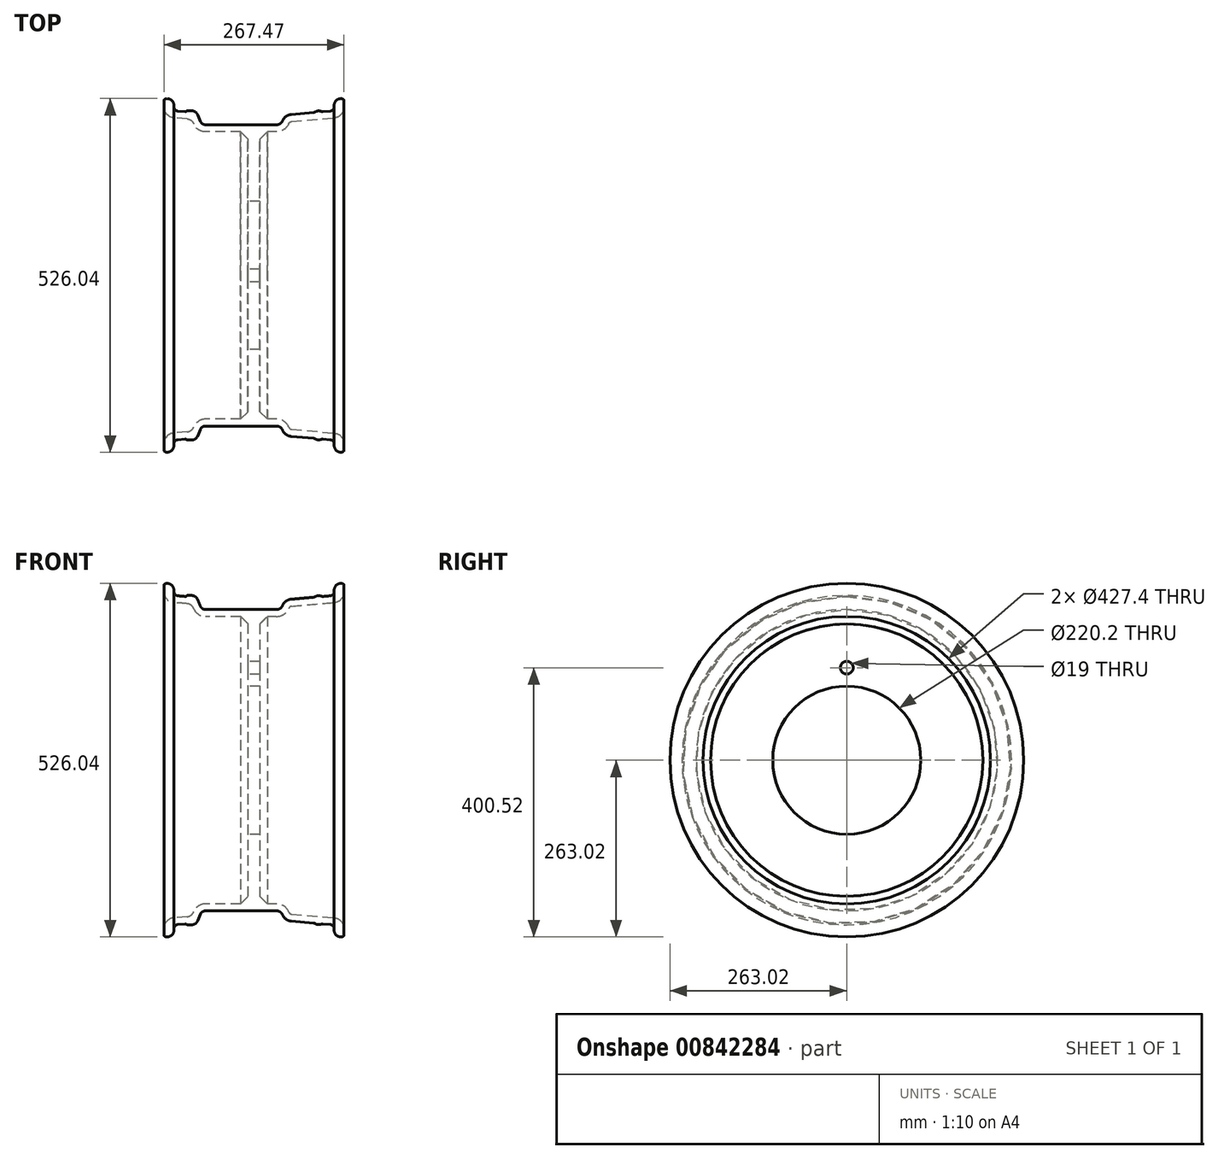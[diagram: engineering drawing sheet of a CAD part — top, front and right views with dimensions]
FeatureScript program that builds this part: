
annotation { "Feature Type Name" : "Feature", "Feature Type Description" : "" }
export const myFeature = defineFeature(function(context is Context, id is Id, definition is map)
    precondition{}
    {
        {
            var Q0;
            Q0=qCreatedBy(makeId("Front.planeOp"),FACE);
            var sketch = newSketch(context, id + "F0", { "sketchPlane" : qUnion([Q0])});
            skArc(sketch, "E0", {"start": v(-59.38, 126.45) * mm, "mid": v(-60.86, 130.03) * mm, "end": v(-64.44, 131.51) * mm});
            skArc(sketch, "E1", {"start": v(-64.44, 131.51) * mm, "mid": v(-65.43, 131.36) * mm, "end": v(-66.34, 130.91) * mm});
            skArc(sketch, "E2", {"start": v(-66.34, 130.91) * mm, "mid": v(-66.59, 130.63) * mm, "end": v(-66.68, 130.27) * mm});
            skArc(sketch, "E3", {"start": v(-66.68, 125.06) * mm, "mid": v(-64.62, 119.78) * mm, "end": v(-59.54, 117.27) * mm});
            skLineSegment(sketch, "E4", {"start": v(-59.54, 117.27) * mm, "end": v(-49.6, 116.4) * mm});
            skArc(sketch, "E5", {"start": v(-44.62, 112.72) * mm, "mid": v(-46.59, 115.26) * mm, "end": v(-49.6, 116.4) * mm});
            skArc(sketch, "E6", {"start": v(-44.62, 112.72) * mm, "mid": v(-41.16, 108.45) * mm, "end": v(-35.91, 106.85) * mm});
            skLineSegment(sketch, "E7", {"start": v(-39.78, 114.67) * mm, "end": v(-41.66, 119.33) * mm});
            skArc(sketch, "E8", {"start": v(-41.66, 119.33) * mm, "mid": v(-43.52, 121.63) * mm, "end": v(-46.35, 122.5) * mm});
            skLineSegment(sketch, "E9", {"start": v(-49.21, 122.5) * mm, "end": v(-46.35, 122.5) * mm});
            skArc(sketch, "E10", {"start": v(-49.21, 122.5) * mm, "mid": v(-49.52, 122.43) * mm, "end": v(-49.78, 122.25) * mm});
            skArc(sketch, "E11", {"start": v(-51.05, 121.76) * mm, "mid": v(-50.36, 121.86) * mm, "end": v(-49.78, 122.25) * mm});
            skLineSegment(sketch, "E12", {"start": v(-56.52, 122.24) * mm, "end": v(-51.05, 121.76) * mm});
            skArc(sketch, "E13", {"start": v(-59.38, 125.36) * mm, "mid": v(-58.56, 123.25) * mm, "end": v(-56.52, 122.24) * mm});
            skArc(sketch, "E14", {"start": v(56.9, 122.24) * mm, "mid": v(58.94, 123.25) * mm, "end": v(59.76, 125.36) * mm});
            skLineSegment(sketch, "E15", {"start": v(51.55, 121.77) * mm, "end": v(56.9, 122.24) * mm});
            skArc(sketch, "E16", {"start": v(50.11, 121.99) * mm, "mid": v(50.82, 121.8) * mm, "end": v(51.55, 121.77) * mm});
            skArc(sketch, "E17", {"start": v(50.11, 121.99) * mm, "mid": v(47.86, 122.32) * mm, "end": v(45.7, 121.6) * mm});
            skArc(sketch, "E18", {"start": v(44.33, 121.14) * mm, "mid": v(45.05, 121.3) * mm, "end": v(45.7, 121.6) * mm});
            skLineSegment(sketch, "E19", {"start": v(27.86, 119.7) * mm, "end": v(44.33, 121.14) * mm});
            skArc(sketch, "E20", {"start": v(27.86, 119.7) * mm, "mid": v(23.94, 118.23) * mm, "end": v(21.33, 114.94) * mm});
            skArc(sketch, "E21", {"start": v(17, 112.06) * mm, "mid": v(19.6, 112.85) * mm, "end": v(21.33, 114.94) * mm});
            skArc(sketch, "E22", {"start": v(16.94, 106.85) * mm, "mid": v(22.43, 108.5) * mm, "end": v(26.08, 112.92) * mm});
            skArc(sketch, "E23", {"start": v(28.25, 114.5) * mm, "mid": v(26.94, 114.01) * mm, "end": v(26.08, 112.92) * mm});
            skLineSegment(sketch, "E24", {"start": v(59.92, 117.27) * mm, "end": v(28.25, 114.5) * mm});
            skArc(sketch, "E25", {"start": v(59.92, 117.27) * mm, "mid": v(65, 119.78) * mm, "end": v(67.06, 125.06) * mm});
            skArc(sketch, "E26", {"start": v(67.06, 130.27) * mm, "mid": v(66.97, 130.63) * mm, "end": v(66.73, 130.91) * mm});
            skArc(sketch, "E27", {"start": v(66.73, 130.91) * mm, "mid": v(65.82, 131.36) * mm, "end": v(64.82, 131.51) * mm});
            skArc(sketch, "E28", {"start": v(64.82, 131.51) * mm, "mid": v(61.24, 130.03) * mm, "end": v(59.76, 126.45) * mm});
            skLineSegment(sketch, "E29", {"start": v(-35.91, 112.06) * mm, "end": v(17, 112.06) * mm});
            skArc(sketch, "E30", {"start": v(-39.78, 114.67) * mm, "mid": v(-38.25, 112.78) * mm, "end": v(-35.91, 112.06) * mm});
            skLineSegment(sketch, "E31", {"start": v(67.06, 130.27) * mm, "end": v(67.06, 125.06) * mm});
            skLineSegment(sketch, "E32", {"start": v(59.76, 125.36) * mm, "end": v(59.76, 126.45) * mm});
            skLineSegment(sketch, "E33", {"start": v(-66.68, 125.06) * mm, "end": v(-66.68, 130.27) * mm});
            skLineSegment(sketch, "E34", {"start": v(-59.38, 126.45) * mm, "end": v(-59.38, 125.36) * mm});
            skLineSegment(sketch, "E35", {"start": v(-4.5, 101.64) * mm, "end": v(-9.71, 106.85) * mm});
            skLineSegment(sketch, "E36", {"start": v(4.5, 101.25) * mm, "end": v(10.1, 106.85) * mm});
            skLineSegment(sketch, "E37", {"start": v(4.89, 101.64) * mm, "end": v(10.1, 106.85) * mm});
            skLineSegment(sketch, "E38", {"start": v(-65.9, 121.68) * mm, "end": v(-65.83, 121.76) * mm});
            skLineSegment(sketch, "E39", {"start": v(-35.91, 106.85) * mm, "end": v(16.94, 106.85) * mm});
            skLineSegment(sketch, "E40", {"start": v(-4.5, 55.05) * mm, "end": v(4.5, 55.05) * mm});
            skLineSegment(sketch, "E41", {"start": v(4.5, 55.05) * mm, "end": v(4.5, 106.85) * mm});
            skLineSegment(sketch, "E42", {"start": v(-4.5, 55.05) * mm, "end": v(-4.5, 106.85) * mm});
            skLineSegment(sketch, "E43", {"start": v(-50, 0) * mm, "end": v(50, 0) * mm, "construction": true});
            skSolve(sketch);
        }
        {
            var Q0;
            Q0 = qSketchRegion(id + "F0", true);
            var Q1;
            Q1=sQuery(id+"F0.wireOp",EDGE,"E43");
            revolve(context, id + "F1", {"surfaceOperationType" : NewSurfaceOperationType.NEW, "entities" : qUnion([Q0]), "axis" : qUnion([Q1]), "revolveType" : RevolveType.FULL});
        }
        {
            var Q0;
            Q0=makeQuery(id+"F1.opRevolve","SWEPT_BODY",BODY,{"disambiguationData":[OSD([sQuery(id+"F0.wireOp",EDGE,"E0"),sQuery(id+"F0.wireOp",EDGE,"E1"),sQuery(id+"F0.wireOp",EDGE,"E2"),sQuery(id+"F0.wireOp",EDGE,"E3"),sQuery(id+"F0.wireOp",EDGE,"E4"),sQuery(id+"F0.wireOp",EDGE,"E5"),sQuery(id+"F0.wireOp",EDGE,"E6"),sQuery(id+"F0.wireOp",EDGE,"E7"),sQuery(id+"F0.wireOp",EDGE,"E8"),sQuery(id+"F0.wireOp",EDGE,"E9"),sQuery(id+"F0.wireOp",EDGE,"E10"),sQuery(id+"F0.wireOp",EDGE,"E11"),sQuery(id+"F0.wireOp",EDGE,"E12"),sQuery(id+"F0.wireOp",EDGE,"E13"),sQuery(id+"F0.wireOp",EDGE,"E14"),sQuery(id+"F0.wireOp",EDGE,"E15"),sQuery(id+"F0.wireOp",EDGE,"E16"),sQuery(id+"F0.wireOp",EDGE,"E17"),sQuery(id+"F0.wireOp",EDGE,"E18"),sQuery(id+"F0.wireOp",EDGE,"E19"),sQuery(id+"F0.wireOp",EDGE,"E20"),sQuery(id+"F0.wireOp",EDGE,"E21"),sQuery(id+"F0.wireOp",EDGE,"E22"),sQuery(id+"F0.wireOp",EDGE,"E23"),sQuery(id+"F0.wireOp",EDGE,"E24"),sQuery(id+"F0.wireOp",EDGE,"E25"),sQuery(id+"F0.wireOp",EDGE,"E26"),sQuery(id+"F0.wireOp",EDGE,"E27"),sQuery(id+"F0.wireOp",EDGE,"E28"),sQuery(id+"F0.wireOp",EDGE,"E29"),sQuery(id+"F0.wireOp",EDGE,"E30"),sQuery(id+"F0.wireOp",EDGE,"E31"),sQuery(id+"F0.wireOp",EDGE,"E32"),sQuery(id+"F0.wireOp",EDGE,"E33"),sQuery(id+"F0.wireOp",EDGE,"E34"),sQuery(id+"F0.wireOp",EDGE,"E35"),sQuery(id+"F0.wireOp",EDGE,"E39"),sQuery(id+"F0.wireOp",EDGE,"E40"),sQuery(id+"F0.wireOp",EDGE,"E41"),sQuery(id+"F0.wireOp",EDGE,"E42")])]});
            var Q1;
            Q1=qCreatedBy(makeId("Origin.pointOp"),VERTEX);
            transform(context, id + "F2", {"entities" : qUnion([Q0]), "transformType" : TransformType.SCALE_UNIFORMLY, "scale" : 2, "scalePoint" : qUnion([Q1]), "makeCopy" : false});
        }
        {
            var Q0;
            Q0=makeQuery(id+"F1.opRevolve","SWEPT_FACE",FACE,{"disambiguationData":[OSD([sQuery(id+"F0.wireOp",EDGE,"E42")])]});
            var sketch = newSketch(context, id + "F3", { "sketchPlane" : qUnion([Q0])});
            skPoint(sketch, "E44", {"position": v(0, 137.5) * mm});
            skSolve(sketch);
        }
        {
            var Q0;
            Q0=sQuery(id+"F3.wireOp",VERTEX,"E44");
            var Q1;
            Q1=makeQuery(id+"F1.opRevolve","SWEPT_BODY",BODY,{"disambiguationData":[OSD([sQuery(id+"F0.wireOp",EDGE,"E0"),sQuery(id+"F0.wireOp",EDGE,"E1"),sQuery(id+"F0.wireOp",EDGE,"E2"),sQuery(id+"F0.wireOp",EDGE,"E3"),sQuery(id+"F0.wireOp",EDGE,"E4"),sQuery(id+"F0.wireOp",EDGE,"E5"),sQuery(id+"F0.wireOp",EDGE,"E6"),sQuery(id+"F0.wireOp",EDGE,"E7"),sQuery(id+"F0.wireOp",EDGE,"E8"),sQuery(id+"F0.wireOp",EDGE,"E9"),sQuery(id+"F0.wireOp",EDGE,"E10"),sQuery(id+"F0.wireOp",EDGE,"E11"),sQuery(id+"F0.wireOp",EDGE,"E12"),sQuery(id+"F0.wireOp",EDGE,"E13"),sQuery(id+"F0.wireOp",EDGE,"E14"),sQuery(id+"F0.wireOp",EDGE,"E15"),sQuery(id+"F0.wireOp",EDGE,"E16"),sQuery(id+"F0.wireOp",EDGE,"E17"),sQuery(id+"F0.wireOp",EDGE,"E18"),sQuery(id+"F0.wireOp",EDGE,"E19"),sQuery(id+"F0.wireOp",EDGE,"E20"),sQuery(id+"F0.wireOp",EDGE,"E21"),sQuery(id+"F0.wireOp",EDGE,"E22"),sQuery(id+"F0.wireOp",EDGE,"E23"),sQuery(id+"F0.wireOp",EDGE,"E24"),sQuery(id+"F0.wireOp",EDGE,"E25"),sQuery(id+"F0.wireOp",EDGE,"E26"),sQuery(id+"F0.wireOp",EDGE,"E27"),sQuery(id+"F0.wireOp",EDGE,"E28"),sQuery(id+"F0.wireOp",EDGE,"E29"),sQuery(id+"F0.wireOp",EDGE,"E30"),sQuery(id+"F0.wireOp",EDGE,"E31"),sQuery(id+"F0.wireOp",EDGE,"E32"),sQuery(id+"F0.wireOp",EDGE,"E33"),sQuery(id+"F0.wireOp",EDGE,"E34"),sQuery(id+"F0.wireOp",EDGE,"E35"),sQuery(id+"F0.wireOp",EDGE,"E39"),sQuery(id+"F0.wireOp",EDGE,"E40"),sQuery(id+"F0.wireOp",EDGE,"E41"),sQuery(id+"F0.wireOp",EDGE,"E42")])]});
            hole(context, id + "F4", {"style" : HoleStyle.SIMPLE, "endStyle" : HoleEndStyle.THROUGH, "holeDiameter" : 19 * mm, "majorDiameter" : 5 * mm, "isTappedThrough" : true, "tappedDepth" : 44 * mm, "tapClearance" : 3, "startFromSketch" : true, "locations" : qUnion([Q0]), "scope" : qUnion([Q1])});
        }
    });
